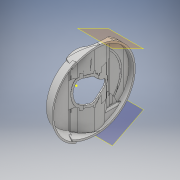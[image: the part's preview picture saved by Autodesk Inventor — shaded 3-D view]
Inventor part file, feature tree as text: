
AUTODESK INVENTOR PART (.ipt)
format: ipt  version: 2018 (Build 220112000, 112)  size: 2,252,800 bytes
history: native  units: mm
features: sketch x62, extrude x56, fillet x13, plane x2, revolve x1, mirror x1
ambient origin geometry x8: Origin, YZ Plane, XZ Plane, XY Plane, X Axis, Y Axis, Z Axis, Center Point
bodies: Solid1 (feature_tree)
feature tree (135):
  extrude  "Extrusion1"  TaperAngle=0.0deg  [1 undecoded]
  extrude  "Extrusion2"  Depth=10.0mm TaperAngle=0.0deg
  extrude  "Extrusion3"  Depth=10.0mm
  extrude  "Extrusion4"  TaperAngle=0.0deg  [1 undecoded]
  extrude  "Extrusion5"  Depth=10.0mm TaperAngle=0.0deg
  sketch  "Sketch6"  dims[d19=10.0mm d20=0.0mm d21=40.0mm]
  extrude  "Extrusion6"  Depth=10.0mm
  extrude  "Extrusion7"  Depth=11.0mm TaperAngle=0.0deg
  extrude  "Extrusion8"  Depth=32.0mm TaperAngle=0.0deg
  extrude  "Extrusion9"  Depth=32.0mm TaperAngle=0.0deg
  extrude  "Extrusion10"  Depth=10.0mm TaperAngle=0.0deg
  extrude  "Extrusion11"  Depth=10.0mm TaperAngle=0.0deg
  extrude  "Extrusion12"  TaperAngle=0.0deg  [1 undecoded]
  extrude  "Extrusion14"  Depth=48.3mm
  extrude  "Extrusion15"  TaperAngle=0.0deg  [1 undecoded]
  extrude  "Extrusion16"  Depth=10.0mm TaperAngle=0.0deg
  extrude  "Extrusion17"  Depth=11.63mm TaperAngle=0.0deg
  sketch  "Sketch21"  dims[d83=0.0mm d84=0.0mm d85=0.0mm d86=0.0mm]
  extrude  "Extrusion19"  Depth=11.63mm TaperAngle=0.0deg
  extrude  "Extrusion20"  TaperAngle=0.0deg  [1 undecoded]
  extrude  "Extrusion21"  Depth=10.0mm TaperAngle=0.0deg
  extrude  "Extrusion22"  TaperAngle=0.0deg  [1 undecoded]
  extrude  "Extrusion23"  Depth=2.86mm TaperAngle=0.0deg
  extrude  "Extrusion24"  Depth=2.01mm
  extrude  "Extrusion25"  Depth=10.0mm TaperAngle=0.0deg
  sketch  "Sketch33"  dims[d115=7.8mm d116=0.0mm d117=0.0mm d118=0.0mm]
  extrude  "Extrusion26"  Depth=10.0mm TaperAngle=0.0deg
  extrude  "Extrusion27"  TaperAngle=0.0deg  [1 undecoded]
  extrude  "Extrusion28"  Depth=16.0mm TaperAngle=0.0deg
  extrude  "Extrusion29"  Depth=17.0mm TaperAngle=0.0deg
  extrude  "Extrusion30"  Depth=2.0mm
  extrude  "Extrusion31"  Depth=2.0mm TaperAngle=0.0deg
  extrude  "Extrusion32"  Depth=18.0mm TaperAngle=0.0deg
  extrude  "Extrusion33"  Depth=16.0mm
  sketch  "Sketch42"  dims[d151=2.0mm d152=2.0mm]
  extrude  "Extrusion34"  Depth=7.72mm TaperAngle=0.0deg
  extrude  "Extrusion36"  Depth=2.0mm
  extrude  "Extrusion37"  Depth=2.0mm
  revolve  "Revolution3"  [1 undecoded]
  extrude  "Extrusion38"  Depth=2.0mm
  extrude  "Extrusion39"  Depth=10.0mm TaperAngle=0.0deg
  fillet  "Fillet1"  Radius=7.83mm
  fillet  "Fillet2"  Radius=20.0mm
  sketch  "Sketch51"
  extrude  "Extrusion41"  [1 undecoded]
  mirror  "Mirror1"
  extrude  "Extrusion42"  [1 undecoded]
  sketch  "Sketch54"
  sketch  "Sketch55"
  sketch  "Sketch56"
  extrude  "Extrusion44"  [1 undecoded]
  extrude  "Extrusion45"  [1 undecoded]
  extrude  "Extrusion46"  [1 undecoded]
  extrude  "Extrusion47"  [1 undecoded]
  plane  "Work Plane2"
  extrude  "Extrusion48"  [1 undecoded]
  extrude  "Extrusion49"  [1 undecoded]
  plane  "Work Plane5"
  extrude  "Extrusion50"  [1 undecoded]
  extrude  "Extrusion51"  [1 undecoded]
  fillet  "Fillet3"  [1 undecoded]
  fillet  "Fillet4"  [1 undecoded]
  extrude  "Extrusion52"  [1 undecoded]
  extrude  "Extrusion53"  [1 undecoded]
  extrude  "Extrusion54"  [1 undecoded]
  extrude  "Extrusion55"  [1 undecoded]
  fillet  "Fillet5"  [1 undecoded]
  extrude  "Extrusion57"  [1 undecoded]
  extrude  "Extrusion58"  [1 undecoded]
  extrude  "Extrusion59"  [1 undecoded]
  fillet  "Fillet7"  [1 undecoded]
  fillet  "Fillet8"  [1 undecoded]
  fillet  "Fillet9"  [1 undecoded]
  fillet  "Fillet10"  [1 undecoded]
  fillet  "Fillet11"  [1 undecoded]
  fillet  "Fillet12"  [1 undecoded]
  fillet  "Fillet13"  [1 undecoded]
  fillet  "Fillet14"  [1 undecoded]
  extrude  "Extrusion60"  [1 undecoded]
  extrude  "Extrusion61"  [1 undecoded]
  extrude  "Extrusion62"  [1 undecoded]
  sketch  "Sketch1"  dims[d0=10.0mm d1=0.0mm d2=0.0mm d3=0.0mm]
  sketch  "Sketch2"  dims[d4=0.0mm d5=0.0mm d6=10.0mm d7=0.0mm]
  sketch  "Sketch3"  dims[d8=10.0mm d9=0.0mm d10=50.0mm]
  sketch  "Sketch4"  dims[d11=10.0mm d12=0.0mm d13=0.0mm d14=0.0mm]
  sketch  "Sketch5"  dims[d15=0.0mm d16=0.0mm d17=10.0mm d18=0.0mm]
  sketch  "Sketch7"  dims[d22=38.0mm d23=11.0mm d24=0.0mm]
  sketch  "Sketch8"  dims[d25=9.5mm d26=0.0mm d33=32.0mm d34=0.0mm]
  sketch  "Sketch9"  dims[d37=32.0mm d38=0.0mm d39=32.0mm d40=0.0mm]
  sketch  "Sketch10"  dims[d41=32.0mm d42=0.0mm d45=10.0mm d46=0.0mm]
  sketch  "Sketch11"  dims[d47=10.0mm d48=0.0mm d49=10.0mm d50=0.0mm]
  sketch  "Sketch12"  dims[d51=0.0mm d52=0.0mm d53=0.0mm d54=0.0mm]
  sketch  "Sketch13"  dims[d65=46.0mm d66=48.3mm]
  sketch  "Sketch16"  dims[d67=9.0mm d68=0.0mm d69=0.0mm d70=0.0mm]
  sketch  "Sketch18"  dims[d71=0.0mm d72=0.0mm d73=10.0mm d74=0.0mm]
  sketch  "Sketch19"  dims[d75=5.0mm d76=0.0mm d77=11.63mm d78=0.0mm]
  sketch  "Sketch20"  dims[d79=11.63mm d80=0.0mm d81=11.63mm d82=0.0mm]
  sketch  "Sketch22"  dims[d87=30.0mm d88=10.0mm d89=0.0mm]
  sketch  "Sketch23"  dims[d92=10.0mm d93=0.0mm d94=0.0mm d95=0.0mm]
  sketch  "Sketch24"  dims[d96=135.0deg d99=2.86mm d100=0.0mm]
  sketch  "Sketch25"  dims[d101=0.0mm d102=0.0mm d105=2.01mm]
  sketch  "Sketch31"  dims[d106=2.22mm d107=10.0mm d108=0.0mm]
  sketch  "Sketch32"  dims[d109=10.0mm d110=0.0mm d113=7.8mm d114=0.0mm]
  sketch  "Sketch34"  dims[d119=16.0mm d120=0.0mm d121=22.0mm d122=0.0mm]
  sketch  "Sketch35"  dims[d123=22.0mm d124=0.0mm d126=17.0mm d127=0.0mm]
  sketch  "Sketch36"  dims[d128=17.0mm d129=0.0mm d130=2.0mm]
  sketch  "Sketch37"  dims[d131=2.0mm d132=6.95mm d133=0.0mm]
  sketch  "Sketch38"  dims[d134=6.95mm d135=0.0mm d136=18.0mm d137=0.0mm]
  sketch  "Sketch39"  dims[d138=16.0mm d139=0.0mm d140=1.02mm]
  sketch  "Sketch40"  dims[d143=15.5mm d144=0.0mm d146=7.72mm d147=0.0mm]
  sketch  "Sketch41"  dims[d148=17.0mm d149=0.0mm d150=2.0mm]
  sketch  "Sketch43"  dims[d153=2.0mm d154=2.0mm]
  sketch  "Sketch45"  dims[d155=2.0mm d156=2.0mm]
  sketch  "Sketch47"  dims[d157=2.0mm d158=10.0mm d159=0.0mm d160=7.83mm d161=0.0mm d162=20.0mm d163=0.0mm]
  sketch  "Sketch48"
  sketch  "Sketch49"
  sketch  "Sketch52"
  sketch  "Sketch53"
  sketch  "Sketch57"
  sketch  "Sketch60"
  sketch  "Sketch61"
  sketch  "Sketch62"
  sketch  "Sketch63"
  sketch  "Sketch65"
  sketch  "Sketch66"
  sketch  "Sketch67"
  sketch  "Sketch68"
  sketch  "Sketch69"
  sketch  "Sketch70"
  sketch  "Sketch72"
  sketch  "Sketch73"
  sketch  "Sketch74"
  sketch  "Sketch75"
  sketch  "Sketch76"
  sketch  "Sketch78"
note: 39 required parameter values undecoded (feature->parameter linkage not recoverable at this tier; creation-order binding heuristic only, values carry confidence <= 0.55)